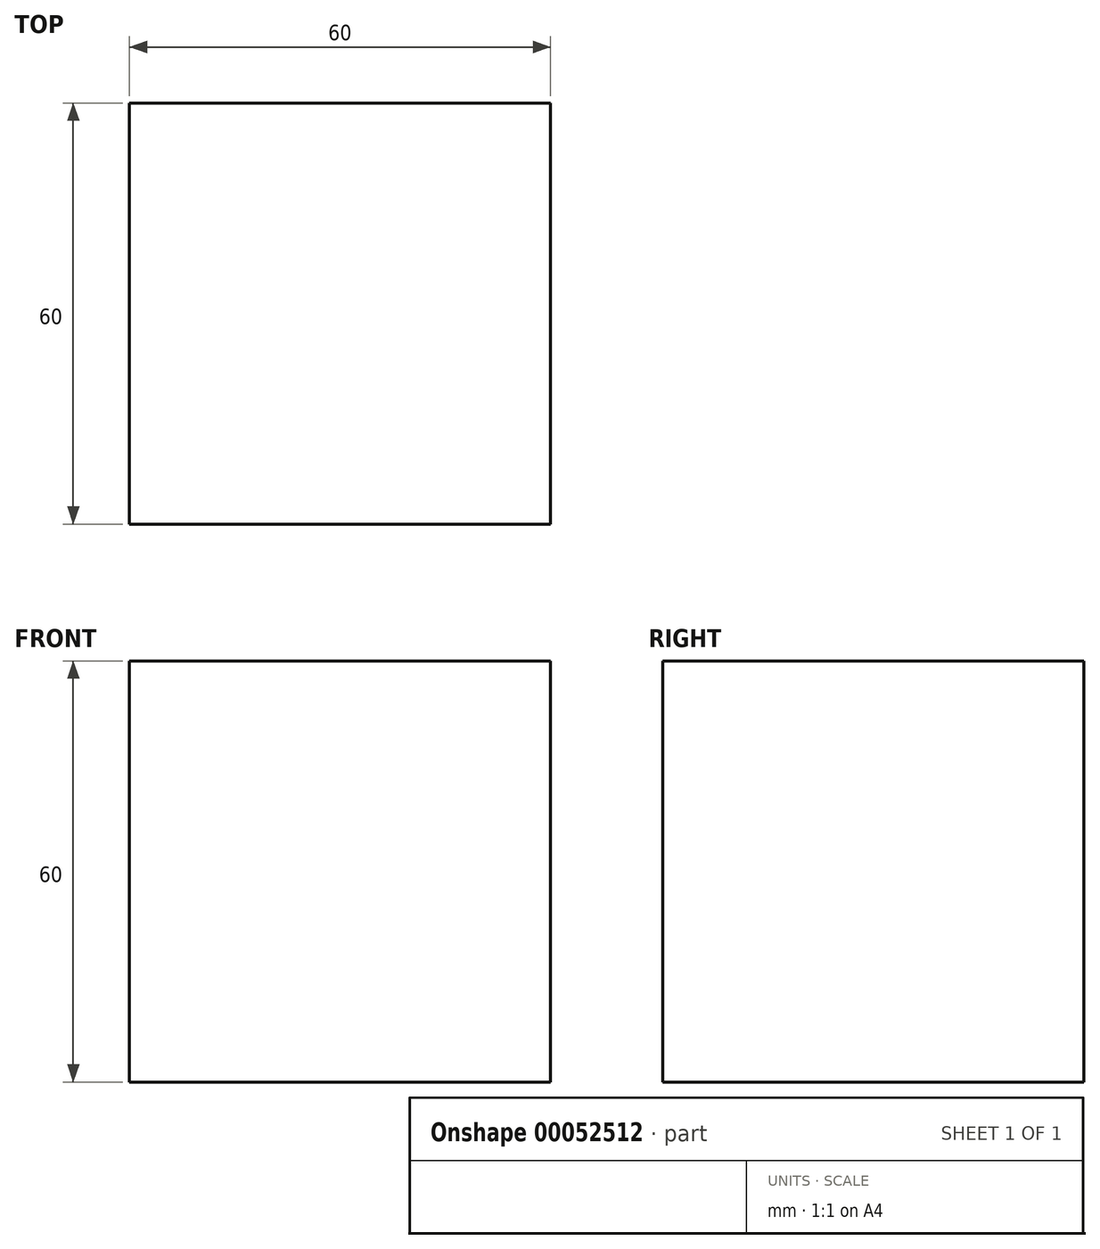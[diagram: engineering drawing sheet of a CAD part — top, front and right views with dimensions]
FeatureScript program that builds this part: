
annotation { "Feature Type Name" : "Feature", "Feature Type Description" : "" }
export const myFeature = defineFeature(function(context is Context, id is Id, definition is map)
    precondition{}
    {
        {
            var Q0;
            Q0=qCreatedBy(makeId("Front.planeOp"),FACE);
            var sketch = newSketch(context, id + "F0", { "sketchPlane" : qUnion([Q0])});
            skLineSegment(sketch, "E0.bottom", {"start": v(0, 0) * mm, "end": v(60, 0) * mm});
            skLineSegment(sketch, "E0.top", {"start": v(0, 60) * mm, "end": v(60, 60) * mm});
            skLineSegment(sketch, "E0.left", {"start": v(0, 0) * mm, "end": v(0, 60) * mm});
            skLineSegment(sketch, "E0.right", {"start": v(60, 0) * mm, "end": v(60, 60) * mm});
            skSolve(sketch);
        }
        {
            var Q0;
            Q0=makeQuery(id+"F0.imprint","IMPRINT",FACE,{"disambiguationData":[TD([[makeQuery(id+"F0.imprint","IMPRINT",EDGE,{"derivedFrom":sQuery(id+"F0.wireOp",EDGE,"E0.bottom")}),1.0]])]});
            extrude(context, id + "F1", {"entities" : qUnion([Q0]), "depth" : 60 * mm});
        }
        {
            var Q0;
            Q0=makeQuery(id+"F1.opExtrude","CAP_FACE",FACE,{"disambiguationData":[OSD([sQuery(id+"F0.wireOp",EDGE,"E0.bottom"),sQuery(id+"F0.wireOp",EDGE,"E0.top"),sQuery(id+"F0.wireOp",EDGE,"E0.left"),sQuery(id+"F0.wireOp",EDGE,"E0.right")])],"isStart":false});
            var sketch = newSketch(context, id + "F2", { "sketchPlane" : qUnion([Q0])});
            skLineSegment(sketch, "E1", {"start": v(30.67, 37.96) * mm, "end": v(0, 37.96) * mm});
            skLineSegment(sketch, "E2", {"start": v(0, 37.96) * mm, "end": v(0, 60) * mm});
            skLineSegment(sketch, "E3", {"start": v(0, 60) * mm, "end": v(30, 60) * mm});
            skLineSegment(sketch, "E4", {"start": v(30, 60) * mm, "end": v(30.67, 37.96) * mm});
            skSolve(sketch);
        }
        {
            var Q0;
            Q0 = qSketchRegion(id + "F2", true);
            extrude(context, id + "F3", {"entities" : qUnion([Q0]), "operationType" : NewBodyOperationType.REMOVE, "depth" : 56.43 * mm});
        }
    });
